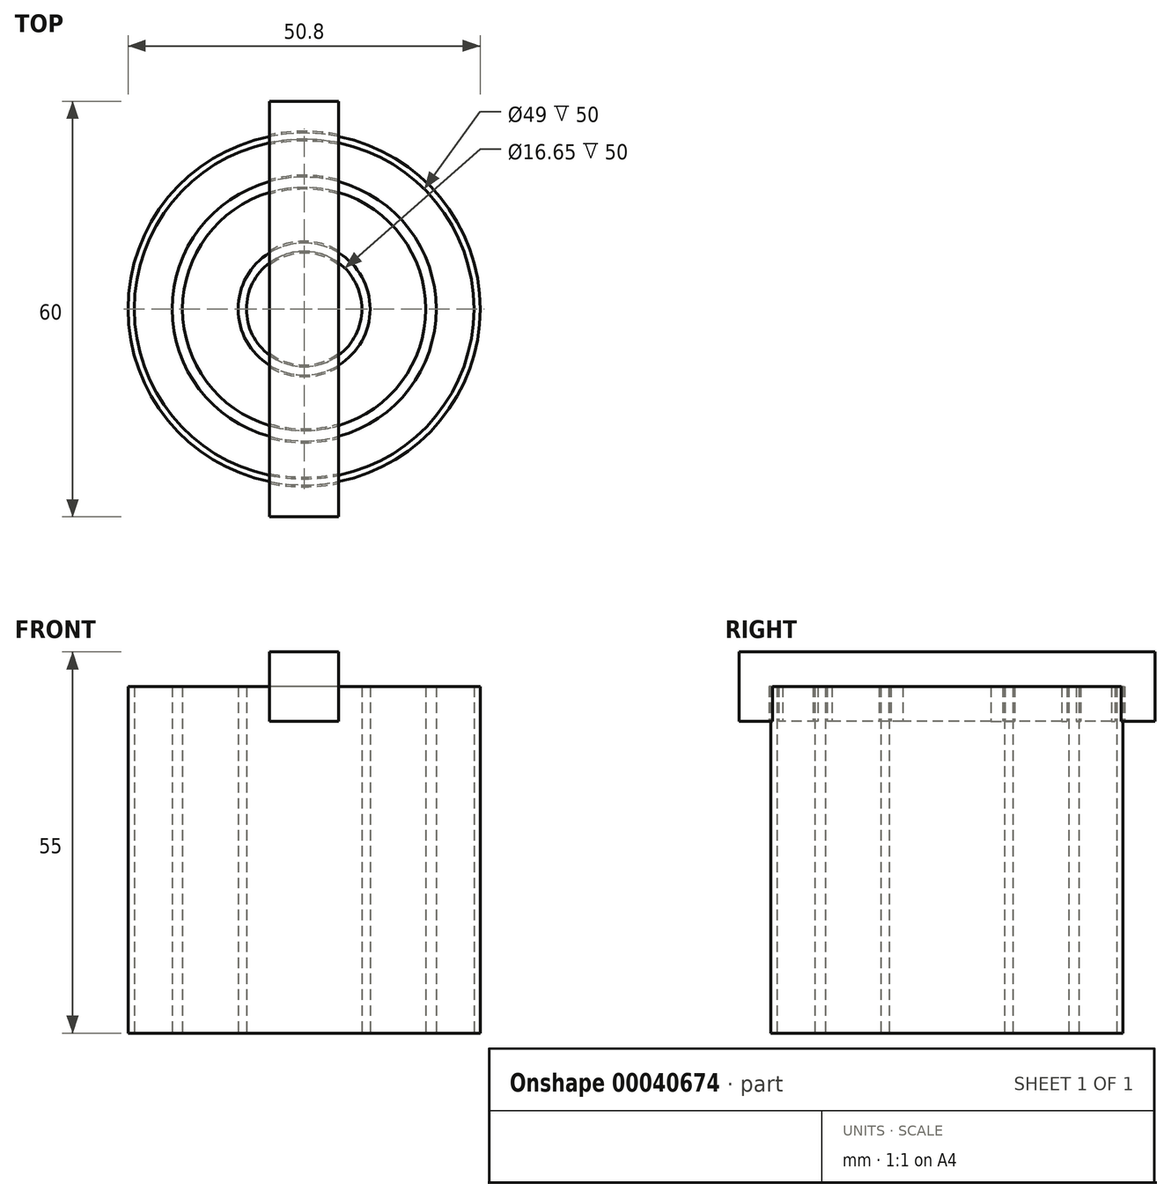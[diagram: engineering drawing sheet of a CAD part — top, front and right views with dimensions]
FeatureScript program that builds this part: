
annotation { "Feature Type Name" : "Feature", "Feature Type Description" : "" }
export const myFeature = defineFeature(function(context is Context, id is Id, definition is map)
    precondition{}
    {
        {
            var Q0;
            Q0=qCreatedBy(makeId("Top.planeOp"),FACE);
            var sketch = newSketch(context, id + "F0", { "sketchPlane" : qUnion([Q0])});
            skCircle(sketch, "E0", {"center": v(0, 0) * mm, "radius": 25.4 * mm});
            skCircle(sketch, "E1", {"center": v(0, 0) * mm, "radius": 19.05 * mm});
            skCircle(sketch, "E2", {"center": v(0, 0) * mm, "radius": 17.55 * mm});
            skCircle(sketch, "E3", {"center": v(0, 0) * mm, "radius": 24.5 * mm});
            skCircle(sketch, "E4", {"center": v(0, 0) * mm, "radius": 9.53 * mm});
            skCircle(sketch, "E5", {"center": v(0, 0) * mm, "radius": 8.33 * mm});
            skSolve(sketch);
        }
        {
            var Q0;
            Q0=makeQuery(id+"F0.imprint","IMPRINT",FACE,{"disambiguationData":[TD([[makeQuery(id+"F0.imprint","IMPRINT",EDGE,{"derivedFrom":sQuery(id+"F0.wireOp",EDGE,"E0")}),1.0]])]});
            var Q1;
            Q1=makeQuery(id+"F0.imprint","IMPRINT",FACE,{"disambiguationData":[TD([[makeQuery(id+"F0.imprint","IMPRINT",EDGE,{"derivedFrom":sQuery(id+"F0.wireOp",EDGE,"E1")}),1.0]])]});
            var Q2;
            Q2=makeQuery(id+"F0.imprint","IMPRINT",FACE,{"disambiguationData":[TD([[makeQuery(id+"F0.imprint","IMPRINT",EDGE,{"derivedFrom":sQuery(id+"F0.wireOp",EDGE,"E4")}),1.0]])]});
            extrude(context, id + "F1", {"entities" : qUnion([Q0, Q1, Q2]), "depth" : 50 * mm});
        }
        {
            var Q0;
            Q0=qCreatedBy(makeId("Top.planeOp"),FACE);
            cPlane(context, id + "F2", {"entities" : qUnion([Q0]), "cplaneType" : CPlaneType.OFFSET, "offset" : 45 * mm, "width" : 150 * mm, "height" : 150 * mm});
        }
        {
            var Q0;
            Q0=qCreatedBy(id+"F2.planeOp",FACE);
            var sketch = newSketch(context, id + "F3", { "sketchPlane" : qUnion([Q0])});
            skLineSegment(sketch, "E6.bottom", {"start": v(-5, 30) * mm, "end": v(5, 30) * mm});
            skLineSegment(sketch, "E6.top", {"start": v(-5, -30) * mm, "end": v(5, -30) * mm});
            skLineSegment(sketch, "E6.left", {"start": v(-5, 30) * mm, "end": v(-5, -30) * mm});
            skLineSegment(sketch, "E6.right", {"start": v(5, 30) * mm, "end": v(5, -30) * mm});
            skLineSegment(sketch, "E7", {"start": v(0, 0) * mm, "end": v(0, -22.27) * mm, "construction": true});
            skPoint(sketch, "E8", {"position": v(0, -30) * mm});
            skLineSegment(sketch, "E9", {"start": v(0, 0) * mm, "end": v(31.54, 0) * mm, "construction": true});
            skPoint(sketch, "E10", {"position": v(5, 0) * mm});
            skSolve(sketch);
        }
        {
            var Q0;
            Q0 = qSketchRegion(id + "F3", true);
            extrude(context, id + "F4", {"entities" : qUnion([Q0]), "depth" : 10 * mm});
        }
        {
            var Q0;
            Q0=makeQuery(id+"F1.opExtrude","SWEPT_BODY",BODY,{"disambiguationData":[OSD([sQuery(id+"F0.wireOp",EDGE,"E0"),sQuery(id+"F0.wireOp",EDGE,"E3")])]});
            var Q1;
            Q1=makeQuery(id+"F1.opExtrude","SWEPT_BODY",BODY,{"disambiguationData":[OSD([sQuery(id+"F0.wireOp",EDGE,"E1"),sQuery(id+"F0.wireOp",EDGE,"E2")])]});
            var Q2;
            Q2=makeQuery(id+"F1.opExtrude","SWEPT_BODY",BODY,{"disambiguationData":[OSD([sQuery(id+"F0.wireOp",EDGE,"E4"),sQuery(id+"F0.wireOp",EDGE,"E5")])]});
            var Q3;
            Q3=makeQuery(id+"F4.opExtrude","SWEPT_BODY",BODY,{"disambiguationData":[OSD([sQuery(id+"F3.wireOp",EDGE,"E6.bottom"),sQuery(id+"F3.wireOp",EDGE,"E6.top"),sQuery(id+"F3.wireOp",EDGE,"E6.left"),sQuery(id+"F3.wireOp",EDGE,"E6.right")])]});
            var Q4;
            Q4=makeQuery(id+"F1.opExtrude","SWEPT_FACE",FACE,{"disambiguationData":[OSD([sQuery(id+"F0.wireOp",EDGE,"E0")])]});
            var Q5;
            Q5=makeQuery(id+"F1.opExtrude","SWEPT_FACE",FACE,{"disambiguationData":[OSD([sQuery(id+"F0.wireOp",EDGE,"E3")])]});
            var Q6;
            Q6=makeQuery(id+"F1.opExtrude","SWEPT_FACE",FACE,{"disambiguationData":[OSD([sQuery(id+"F0.wireOp",EDGE,"E1")])]});
            var Q7;
            Q7=makeQuery(id+"F1.opExtrude","SWEPT_FACE",FACE,{"disambiguationData":[OSD([sQuery(id+"F0.wireOp",EDGE,"E2")])]});
            var Q8;
            Q8=makeQuery(id+"F1.opExtrude","SWEPT_FACE",FACE,{"disambiguationData":[OSD([sQuery(id+"F0.wireOp",EDGE,"E4")])]});
            var Q9;
            Q9=makeQuery(id+"F1.opExtrude","SWEPT_FACE",FACE,{"disambiguationData":[OSD([sQuery(id+"F0.wireOp",EDGE,"E5")])]});
            booleanBodies(context, id + "F5", {"operationType" : BooleanOperationType.SUBTRACTION, "tools" : qUnion([Q0, Q1, Q2]), "targets" : qUnion([Q3]), "offset" : true, "entitiesToOffset" : qUnion([Q4, Q5, Q6, Q7, Q8, Q9]), "offsetDistance" : 0.25 * mm, "keepTools" : true});
        }
    });
